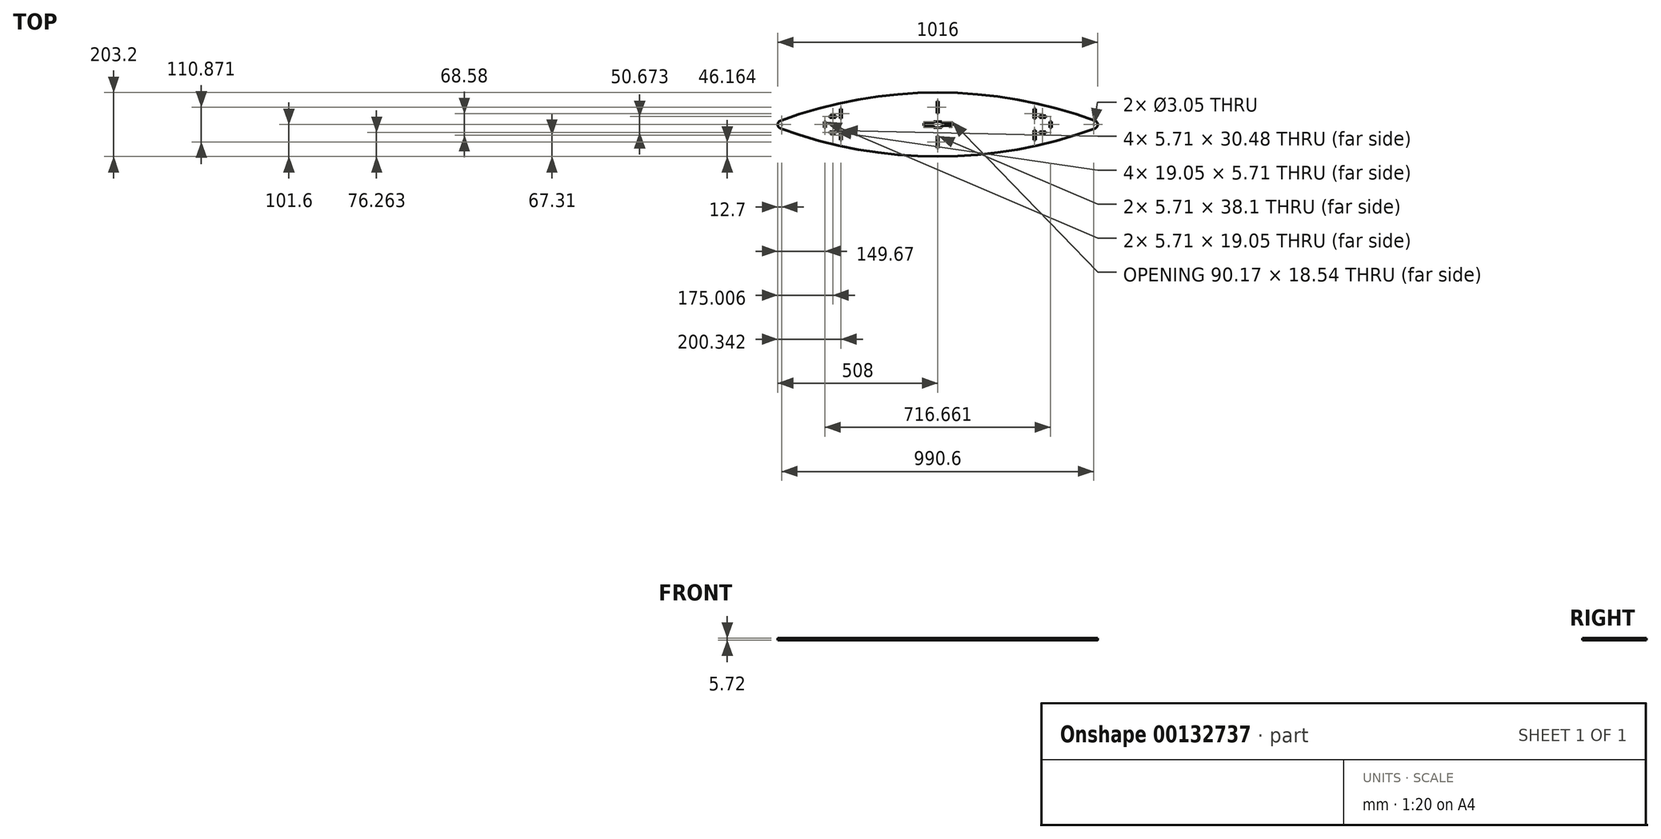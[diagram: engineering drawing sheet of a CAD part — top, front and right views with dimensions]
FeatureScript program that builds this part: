
annotation { "Feature Type Name" : "Feature", "Feature Type Description" : "" }
export const myFeature = defineFeature(function(context is Context, id is Id, definition is map)
    precondition{}
    {
        {
            var Q0;
            Q0=qCreatedBy(makeId("Top.planeOp"),FACE);
            var sketch = newSketch(context, id + "F0", { "sketchPlane" : qUnion([Q0])});
            skArc(sketch, "E0", {"start": v(-499.72, 11.9) * mm, "mid": v(-505.73, 7.25) * mm, "end": v(-508, 0) * mm});
            skLineSegment(sketch, "E1.bottom", {"start": v(-508, 0) * mm, "end": v(508, 0) * mm, "construction": true});
            skLineSegment(sketch, "E1.top", {"start": v(-508, 101.6) * mm, "end": v(508, 101.6) * mm, "construction": true});
            skLineSegment(sketch, "E1.left", {"start": v(-508, 0) * mm, "end": v(-508, 101.6) * mm, "construction": true});
            skLineSegment(sketch, "E1.right", {"start": v(508, 0) * mm, "end": v(508, 101.6) * mm, "construction": true});
            skArc(sketch, "E2", {"start": v(0, 101.6) * mm, "mid": v(-253.85, 79) * mm, "end": v(-499.72, 11.9) * mm});
            skArc(sketch, "E3.MirrorCS", {"start": v(0, 101.6) * mm, "mid": v(253.85, 79) * mm, "end": v(499.72, 11.9) * mm});
            skArc(sketch, "E4.MirrorCS", {"start": v(499.72, 11.9) * mm, "mid": v(505.73, 7.25) * mm, "end": v(508, 0) * mm});
            skArc(sketch, "E5.MirrorCS", {"start": v(499.72, -11.9) * mm, "mid": v(505.73, -7.25) * mm, "end": v(508, 0) * mm});
            skArc(sketch, "E6.MirrorCS", {"start": v(0, -101.6) * mm, "mid": v(253.85, -79) * mm, "end": v(499.72, -11.9) * mm});
            skArc(sketch, "E7.MirrorCS", {"start": v(0, -101.6) * mm, "mid": v(-253.85, -79) * mm, "end": v(-499.72, -11.9) * mm});
            skArc(sketch, "E8.MirrorCS", {"start": v(-499.72, -11.9) * mm, "mid": v(-505.73, -7.25) * mm, "end": v(-508, 0) * mm});
            skSolve(sketch);
        }
        {
            var Q0;
            Q0 = qSketchRegion(id + "F0", true);
            extrude(context, id + "F1", {"entities" : qUnion([Q0]), "depth" : 5.7 * mm});
        }
        {
            var Q0;
            Q0=qCreatedBy(makeId("Front.planeOp"),FACE);
            var sketch = newSketch(context, id + "F2", { "sketchPlane" : qUnion([Q0])});
            skLineSegment(sketch, "E9", {"start": v(0, 0) * mm, "end": v(0, 5.72) * mm, "construction": true});
            skLineSegment(sketch, "E10", {"start": v(0, 5.72) * mm, "end": v(5.72, 5.72) * mm, "construction": true});
            skSolve(sketch);
        }
        {
            var Q0;
            Q0=makeQuery(id+"F1.opExtrude","CAP_FACE",FACE,{"disambiguationData":[OSD([sQuery(id+"F0.wireOp",EDGE,"E0"),sQuery(id+"F0.wireOp",EDGE,"E2"),sQuery(id+"F0.wireOp",EDGE,"E3.MirrorCS"),sQuery(id+"F0.wireOp",EDGE,"E4.MirrorCS"),sQuery(id+"F0.wireOp",EDGE,"E5.MirrorCS"),sQuery(id+"F0.wireOp",EDGE,"E6.MirrorCS"),sQuery(id+"F0.wireOp",EDGE,"E7.MirrorCS"),sQuery(id+"F0.wireOp",EDGE,"E8.MirrorCS")])],"isStart":false});
            var sketch = newSketch(context, id + "F3", { "sketchPlane" : qUnion([Q0])});
            skLineSegment(sketch, "E11", {"start": v(-45.09, 0) * mm, "end": v(-45.09, 3.56) * mm});
            skLineSegment(sketch, "E12", {"start": v(-45.09, 3.56) * mm, "end": v(-12.7, 3.56) * mm});
            skLineSegment(sketch, "E13", {"start": v(-12.7, 3.56) * mm, "end": v(-12.7, 9.27) * mm});
            skLineSegment(sketch, "E14", {"start": v(-12.7, 9.27) * mm, "end": v(0, 9.27) * mm});
            skLineSegment(sketch, "E15", {"start": v(-45.09, 3.56) * mm, "end": v(-39.37, 3.56) * mm, "construction": true});
            skLineSegment(sketch, "E16", {"start": v(-39.37, 3.56) * mm, "end": v(-39.37, 0) * mm, "construction": true});
            skLineSegment(sketch, "E17.MirrorCS", {"start": v(12.7, 9.27) * mm, "end": v(0, 9.27) * mm});
            skLineSegment(sketch, "E18.MirrorCS", {"start": v(12.7, 3.56) * mm, "end": v(12.7, 9.27) * mm});
            skLineSegment(sketch, "E19.MirrorCS", {"start": v(45.09, 0) * mm, "end": v(45.09, 3.56) * mm});
            skLineSegment(sketch, "E20.MirrorCS", {"start": v(45.09, 3.56) * mm, "end": v(12.7, 3.56) * mm});
            skLineSegment(sketch, "E21.MirrorCS", {"start": v(45.09, 0) * mm, "end": v(45.09, -3.56) * mm});
            skLineSegment(sketch, "E22.MirrorCS", {"start": v(45.09, -3.56) * mm, "end": v(12.7, -3.56) * mm});
            skLineSegment(sketch, "E23.MirrorCS", {"start": v(12.7, -3.56) * mm, "end": v(12.7, -9.27) * mm});
            skLineSegment(sketch, "E24.MirrorCS", {"start": v(12.7, -9.27) * mm, "end": v(0, -9.27) * mm});
            skLineSegment(sketch, "E25.MirrorCS", {"start": v(-12.7, -9.27) * mm, "end": v(0, -9.27) * mm});
            skLineSegment(sketch, "E26.MirrorCS", {"start": v(-12.7, -3.56) * mm, "end": v(-12.7, -9.27) * mm});
            skLineSegment(sketch, "E27.MirrorCS", {"start": v(-45.09, 0) * mm, "end": v(-45.09, -3.56) * mm});
            skLineSegment(sketch, "E28.MirrorCS", {"start": v(-45.09, -3.56) * mm, "end": v(-12.7, -3.56) * mm});
            skPoint(sketch, "E29", {"position": v(39.37, 3.56) * mm});
            skSolve(sketch);
        }
        {
            var Q0;
            Q0 = qSketchRegion(id + "F3", true);
            extrude(context, id + "F4", {"entities" : qUnion([Q0]), "operationType" : NewBodyOperationType.REMOVE, "endBound" : BoundingType.THROUGH_ALL, "oppositeDirection" : true, "depth" : 25.4 * mm});
        }
        {
            var Q0;
            Q0=makeQuery(id+"F1.opExtrude","CAP_FACE",FACE,{"disambiguationData":[OSD([sQuery(id+"F0.wireOp",EDGE,"E0"),sQuery(id+"F0.wireOp",EDGE,"E2"),sQuery(id+"F0.wireOp",EDGE,"E3.MirrorCS"),sQuery(id+"F0.wireOp",EDGE,"E4.MirrorCS"),sQuery(id+"F0.wireOp",EDGE,"E5.MirrorCS"),sQuery(id+"F0.wireOp",EDGE,"E6.MirrorCS"),sQuery(id+"F0.wireOp",EDGE,"E7.MirrorCS"),sQuery(id+"F0.wireOp",EDGE,"E8.MirrorCS")])],"isStart":false});
            var sketch = newSketch(context, id + "F5", { "sketchPlane" : qUnion([Q0])});
            skLineSegment(sketch, "E30.bottom", {"start": v(-2.86, 74.49) * mm, "end": v(2.86, 74.49) * mm});
            skLineSegment(sketch, "E30.top", {"start": v(-2.86, 36.39) * mm, "end": v(2.86, 36.39) * mm});
            skLineSegment(sketch, "E30.left", {"start": v(-2.86, 74.49) * mm, "end": v(-2.86, 36.39) * mm});
            skLineSegment(sketch, "E30.right", {"start": v(2.86, 74.49) * mm, "end": v(2.86, 36.39) * mm});
            skLineSegment(sketch, "E31", {"start": v(0, 9.27) * mm, "end": v(0, 101.6) * mm, "construction": true});
            skPoint(sketch, "E32", {"position": v(0, 55.44) * mm});
            skPoint(sketch, "E33", {"position": v(-2.86, 55.44) * mm});
            skLineSegment(sketch, "E34.MirrorCS", {"start": v(-2.86, -36.39) * mm, "end": v(2.86, -36.39) * mm});
            skLineSegment(sketch, "E35.MirrorCS", {"start": v(2.86, -74.49) * mm, "end": v(2.86, -36.39) * mm});
            skLineSegment(sketch, "E36.MirrorCS", {"start": v(-2.86, -74.49) * mm, "end": v(-2.86, -36.39) * mm});
            skLineSegment(sketch, "E37.MirrorCS", {"start": v(-2.86, -74.49) * mm, "end": v(2.86, -74.49) * mm});
            skSolve(sketch);
        }
        {
            var Q0;
            Q0 = qSketchRegion(id + "F5", true);
            extrude(context, id + "F6", {"entities" : qUnion([Q0]), "operationType" : NewBodyOperationType.REMOVE, "endBound" : BoundingType.THROUGH_ALL, "oppositeDirection" : true, "depth" : 25.4 * mm});
        }
        {
            var Q0;
            Q0=makeQuery(id+"F1.opExtrude","CAP_FACE",FACE,{"disambiguationData":[OSD([sQuery(id+"F0.wireOp",EDGE,"E0"),sQuery(id+"F0.wireOp",EDGE,"E2"),sQuery(id+"F0.wireOp",EDGE,"E3.MirrorCS"),sQuery(id+"F0.wireOp",EDGE,"E4.MirrorCS"),sQuery(id+"F0.wireOp",EDGE,"E5.MirrorCS"),sQuery(id+"F0.wireOp",EDGE,"E6.MirrorCS"),sQuery(id+"F0.wireOp",EDGE,"E7.MirrorCS"),sQuery(id+"F0.wireOp",EDGE,"E8.MirrorCS")])],"isStart":false});
            var sketch = newSketch(context, id + "F7", { "sketchPlane" : qUnion([Q0])});
            skLineSegment(sketch, "E38.bottom", {"start": v(-310.52, 49.53) * mm, "end": v(-304.8, 49.53) * mm});
            skLineSegment(sketch, "E38.top", {"start": v(-310.52, 19.05) * mm, "end": v(-304.8, 19.05) * mm});
            skLineSegment(sketch, "E38.left", {"start": v(-310.52, 49.53) * mm, "end": v(-310.52, 19.05) * mm});
            skLineSegment(sketch, "E38.right", {"start": v(-304.8, 49.53) * mm, "end": v(-304.8, 19.05) * mm});
            skLineSegment(sketch, "E39.MirrorCS", {"start": v(-310.52, -19.05) * mm, "end": v(-304.8, -19.05) * mm});
            skLineSegment(sketch, "E40.MirrorCS", {"start": v(-310.52, -49.53) * mm, "end": v(-304.8, -49.53) * mm});
            skLineSegment(sketch, "E41.MirrorCS", {"start": v(-310.52, -49.53) * mm, "end": v(-310.52, -19.05) * mm});
            skLineSegment(sketch, "E42.MirrorCS", {"start": v(-304.8, -49.53) * mm, "end": v(-304.8, -19.05) * mm});
            skLineSegment(sketch, "E43.MirrorCS", {"start": v(310.52, -49.53) * mm, "end": v(304.8, -49.53) * mm});
            skLineSegment(sketch, "E44.MirrorCS", {"start": v(304.8, -49.53) * mm, "end": v(304.8, -19.05) * mm});
            skLineSegment(sketch, "E45.MirrorCS", {"start": v(310.52, -19.05) * mm, "end": v(304.8, -19.05) * mm});
            skLineSegment(sketch, "E46.MirrorCS", {"start": v(310.52, -49.53) * mm, "end": v(310.52, -19.05) * mm});
            skLineSegment(sketch, "E47.MirrorCS", {"start": v(310.52, 19.05) * mm, "end": v(304.8, 19.05) * mm});
            skLineSegment(sketch, "E48.MirrorCS", {"start": v(304.8, 49.53) * mm, "end": v(304.8, 19.05) * mm});
            skLineSegment(sketch, "E49.MirrorCS", {"start": v(310.52, 49.53) * mm, "end": v(310.52, 19.05) * mm});
            skLineSegment(sketch, "E50.MirrorCS", {"start": v(310.52, 49.53) * mm, "end": v(304.8, 49.53) * mm});
            skSolve(sketch);
        }
        {
            var Q0;
            Q0 = qSketchRegion(id + "F7", true);
            extrude(context, id + "F8", {"entities" : qUnion([Q0]), "operationType" : NewBodyOperationType.REMOVE, "endBound" : BoundingType.THROUGH_ALL, "oppositeDirection" : true, "depth" : 25.4 * mm});
        }
        {
            var Q0;
            Q0=makeQuery(id+"F1.opExtrude","CAP_FACE",FACE,{"disambiguationData":[OSD([sQuery(id+"F0.wireOp",EDGE,"E0"),sQuery(id+"F0.wireOp",EDGE,"E2"),sQuery(id+"F0.wireOp",EDGE,"E3.MirrorCS"),sQuery(id+"F0.wireOp",EDGE,"E4.MirrorCS"),sQuery(id+"F0.wireOp",EDGE,"E5.MirrorCS"),sQuery(id+"F0.wireOp",EDGE,"E6.MirrorCS"),sQuery(id+"F0.wireOp",EDGE,"E7.MirrorCS"),sQuery(id+"F0.wireOp",EDGE,"E8.MirrorCS")])],"isStart":false});
            var sketch = newSketch(context, id + "F9", { "sketchPlane" : qUnion([Q0])});
            skLineSegment(sketch, "E51.bottom", {"start": v(-355.47, 22.48) * mm, "end": v(-310.52, 22.48) * mm, "construction": true});
            skLineSegment(sketch, "E51.top", {"start": v(-355.47, -22.48) * mm, "end": v(-310.52, -22.48) * mm, "construction": true});
            skLineSegment(sketch, "E51.left", {"start": v(-355.47, 22.48) * mm, "end": v(-355.47, -22.48) * mm, "construction": true});
            skLineSegment(sketch, "E51.right", {"start": v(-310.52, 22.48) * mm, "end": v(-310.52, -22.48) * mm, "construction": true});
            skLineSegment(sketch, "E52.bottom", {"start": v(-342.52, 22.48) * mm, "end": v(-323.47, 22.48) * mm});
            skLineSegment(sketch, "E52.top", {"start": v(-342.52, 28.2) * mm, "end": v(-323.47, 28.2) * mm});
            skLineSegment(sketch, "E52.left", {"start": v(-342.52, 22.48) * mm, "end": v(-342.52, 28.2) * mm});
            skLineSegment(sketch, "E52.right", {"start": v(-323.47, 22.48) * mm, "end": v(-323.47, 28.2) * mm});
            skLineSegment(sketch, "E53", {"start": v(-333, -22.48) * mm, "end": v(-333, 22.48) * mm, "construction": true});
            skPoint(sketch, "E53.startSnap0", {"position": v(-333, 22.48) * mm});
            skLineSegment(sketch, "E54", {"start": v(-333, 0) * mm, "end": v(-355.47, 0) * mm, "construction": true});
            skLineSegment(sketch, "E55.bottom", {"start": v(-355.47, 9.53) * mm, "end": v(-361.19, 9.53) * mm});
            skLineSegment(sketch, "E55.top", {"start": v(-355.47, -9.53) * mm, "end": v(-361.19, -9.53) * mm});
            skLineSegment(sketch, "E55.left", {"start": v(-355.47, 9.53) * mm, "end": v(-355.47, -9.53) * mm});
            skLineSegment(sketch, "E55.right", {"start": v(-361.19, 9.53) * mm, "end": v(-361.19, -9.53) * mm});
            skPoint(sketch, "E56", {"position": v(-355.47, 0) * mm});
            skLineSegment(sketch, "E57.MirrorCS", {"start": v(-323.47, -22.48) * mm, "end": v(-323.47, -28.2) * mm});
            skLineSegment(sketch, "E58.MirrorCS", {"start": v(-342.52, -28.2) * mm, "end": v(-323.47, -28.2) * mm});
            skLineSegment(sketch, "E59.MirrorCS", {"start": v(-342.52, -22.48) * mm, "end": v(-342.52, -28.2) * mm});
            skLineSegment(sketch, "E60", {"start": v(-342.52, -22.48) * mm, "end": v(-323.47, -22.48) * mm});
            skLineSegment(sketch, "E61.MirrorCS", {"start": v(342.52, -22.48) * mm, "end": v(342.52, -28.2) * mm});
            skLineSegment(sketch, "E62.MirrorCS", {"start": v(323.47, -22.48) * mm, "end": v(323.47, -28.2) * mm});
            skLineSegment(sketch, "E63.MirrorCS", {"start": v(355.47, -9.53) * mm, "end": v(361.19, -9.53) * mm});
            skLineSegment(sketch, "E64.MirrorCS", {"start": v(355.47, 9.53) * mm, "end": v(361.19, 9.53) * mm});
            skLineSegment(sketch, "E65.MirrorCS", {"start": v(342.52, 22.48) * mm, "end": v(342.52, 28.2) * mm});
            skLineSegment(sketch, "E66.MirrorCS", {"start": v(323.47, 22.48) * mm, "end": v(323.47, 28.2) * mm});
            skLineSegment(sketch, "E67.MirrorCS", {"start": v(355.47, 9.53) * mm, "end": v(355.47, -9.53) * mm});
            skPoint(sketch, "E68.MirrorP", {"position": v(355.47, 0) * mm});
            skLineSegment(sketch, "E69.MirrorCS", {"start": v(342.52, -22.48) * mm, "end": v(323.47, -22.48) * mm});
            skLineSegment(sketch, "E70.MirrorCS", {"start": v(361.19, 9.53) * mm, "end": v(361.19, -9.53) * mm});
            skLineSegment(sketch, "E71.MirrorCS", {"start": v(342.52, -28.2) * mm, "end": v(323.47, -28.2) * mm});
            skLineSegment(sketch, "E72.MirrorCS", {"start": v(333, 0) * mm, "end": v(355.47, 0) * mm, "construction": true});
            skPoint(sketch, "E73.MirrorP", {"position": v(333, 22.48) * mm});
            skLineSegment(sketch, "E74.MirrorCS", {"start": v(333, -22.48) * mm, "end": v(333, 22.48) * mm, "construction": true});
            skLineSegment(sketch, "E75.MirrorCS", {"start": v(355.47, 22.48) * mm, "end": v(355.47, -22.48) * mm, "construction": true});
            skLineSegment(sketch, "E76.MirrorCS", {"start": v(342.52, 22.48) * mm, "end": v(323.47, 22.48) * mm});
            skLineSegment(sketch, "E77.MirrorCS", {"start": v(342.52, 28.2) * mm, "end": v(323.47, 28.2) * mm});
            skLineSegment(sketch, "E78.MirrorCS", {"start": v(355.47, -22.48) * mm, "end": v(310.52, -22.48) * mm, "construction": true});
            skLineSegment(sketch, "E79.MirrorCS", {"start": v(355.47, 22.48) * mm, "end": v(310.52, 22.48) * mm, "construction": true});
            skSolve(sketch);
        }
        {
            var Q0;
            Q0 = qSketchRegion(id + "F9", true);
            extrude(context, id + "F10", {"entities" : qUnion([Q0]), "operationType" : NewBodyOperationType.REMOVE, "endBound" : BoundingType.THROUGH_ALL, "oppositeDirection" : true, "depth" : 25.4 * mm});
        }
        {
            var Q0;
            Q0=makeQuery(id+"F1.opExtrude","CAP_FACE",FACE,{"disambiguationData":[OSD([sQuery(id+"F0.wireOp",EDGE,"E0"),sQuery(id+"F0.wireOp",EDGE,"E2"),sQuery(id+"F0.wireOp",EDGE,"E3.MirrorCS"),sQuery(id+"F0.wireOp",EDGE,"E4.MirrorCS"),sQuery(id+"F0.wireOp",EDGE,"E5.MirrorCS"),sQuery(id+"F0.wireOp",EDGE,"E6.MirrorCS"),sQuery(id+"F0.wireOp",EDGE,"E7.MirrorCS"),sQuery(id+"F0.wireOp",EDGE,"E8.MirrorCS")])],"isStart":false});
            var sketch = newSketch(context, id + "F11", { "sketchPlane" : qUnion([Q0])});
            skCircle(sketch, "E80", {"center": v(-495.3, 0) * mm, "radius": 1.52 * mm});
            skCircle(sketch, "E81.MirrorC", {"center": v(495.3, 0) * mm, "radius": 1.52 * mm});
            skSolve(sketch);
        }
        {
            var Q0;
            Q0 = qSketchRegion(id + "F11", true);
            extrude(context, id + "F12", {"entities" : qUnion([Q0]), "operationType" : NewBodyOperationType.REMOVE, "endBound" : BoundingType.THROUGH_ALL, "oppositeDirection" : true, "depth" : 25.4 * mm});
        }
    });
